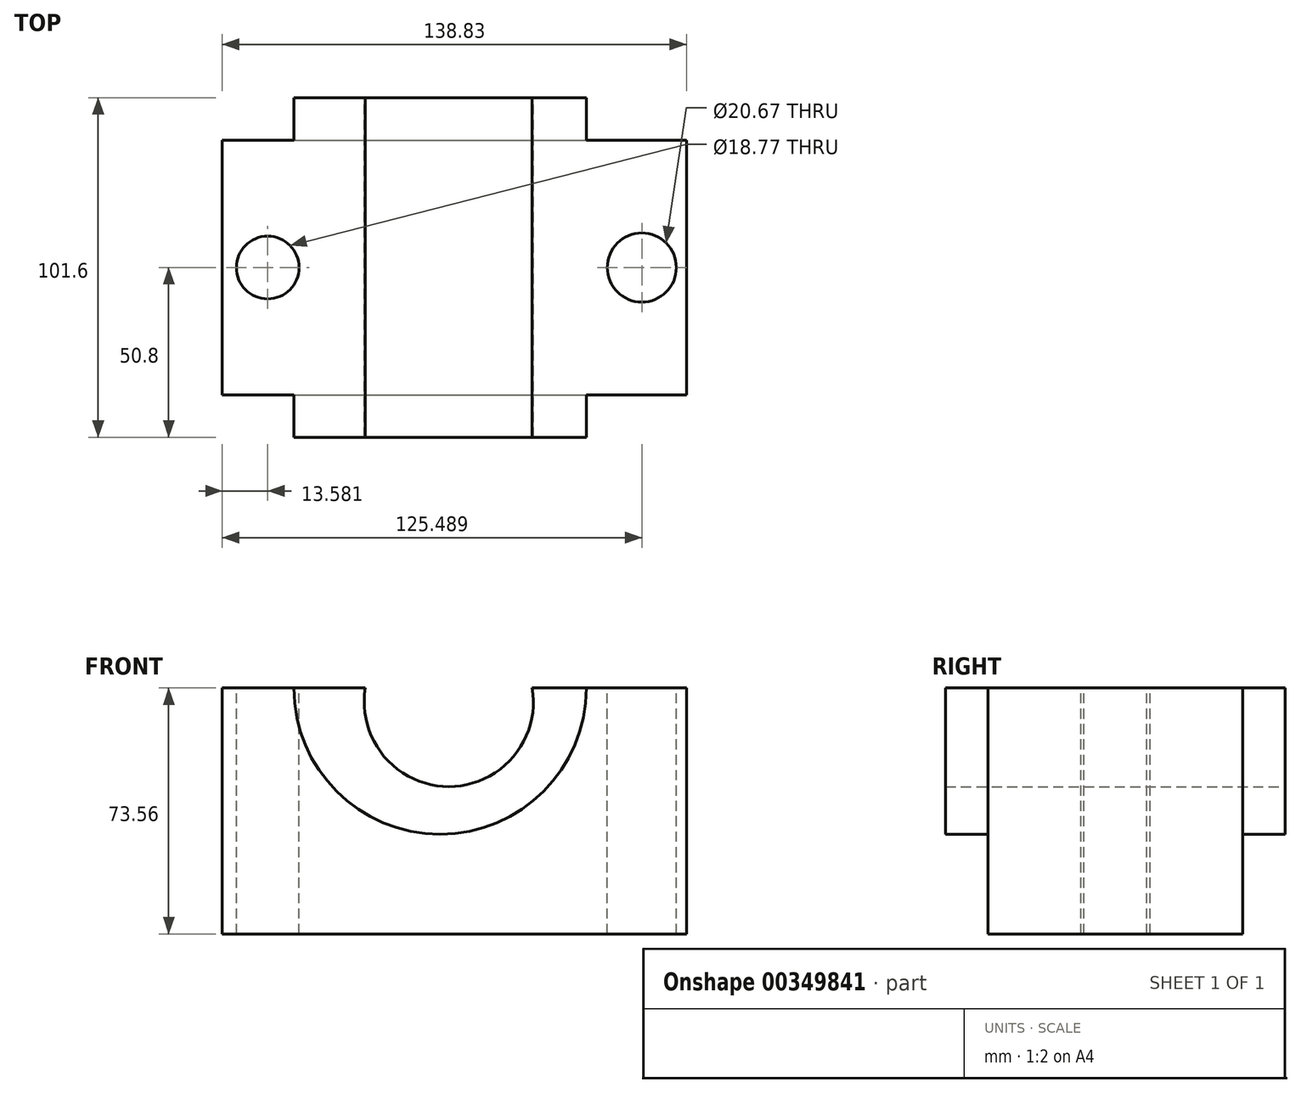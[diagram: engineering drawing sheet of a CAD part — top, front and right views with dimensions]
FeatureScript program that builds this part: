
annotation { "Feature Type Name" : "Feature", "Feature Type Description" : "" }
export const myFeature = defineFeature(function(context is Context, id is Id, definition is map)
    precondition{}
    {
        {
            var Q0;
            Q0=qCreatedBy(makeId("Front.planeOp"),FACE);
            var sketch = newSketch(context, id + "F0", { "sketchPlane" : qUnion([Q0])});
            skLineSegment(sketch, "E0.bottom", {"start": v(-77.5, 11.39) * mm, "end": v(61.33, 11.39) * mm});
            skLineSegment(sketch, "E0.top", {"start": v(-77.5, -62.17) * mm, "end": v(61.33, -62.17) * mm});
            skLineSegment(sketch, "E0.left", {"start": v(-77.5, 11.39) * mm, "end": v(-77.5, -62.17) * mm});
            skLineSegment(sketch, "E0.right", {"start": v(61.33, 11.39) * mm, "end": v(61.33, -62.17) * mm});
            skArc(sketch, "E1", {"start": v(-34.7, 11.39) * mm, "mid": v(-9.75, -18.1) * mm, "end": v(15.21, 11.39) * mm});
            skSolve(sketch);
        }
        {
            var Q0;
            Q0=makeQuery(id+"F0.imprint","IMPRINT",FACE,{"disambiguationData":[TD([[makeQuery(id+"F0.imprint","IMPRINT",EDGE,{"derivedFrom":sQuery(id+"F0.wireOp",EDGE,"E0.top")}),1.0]])]});
            extrude(context, id + "F1", {"entities" : qUnion([Q0]), "depth" : 38.1 * mm, "hasSecondDirection" : true, "secondDirectionOppositeDirection" : true, "secondDirectionDepth" : 38.1 * mm});
        }
        {
            var Q0;
            Q0=qCreatedBy(makeId("Front.planeOp"),FACE);
            var sketch = newSketch(context, id + "F2", { "sketchPlane" : qUnion([Q0])});
            skArc(sketch, "E2.0", {"start": v(-34.7, 11.39) * mm, "mid": v(-9.75, -18.1) * mm, "end": v(15.21, 11.39) * mm});
            skLineSegment(sketch, "E3.0", {"start": v(-77.5, 11.39) * mm, "end": v(-34.7, 11.39) * mm});
            skLineSegment(sketch, "E4.0", {"start": v(15.21, 11.39) * mm, "end": v(61.33, 11.39) * mm});
            skArc(sketch, "E5", {"start": v(-56.1, 11.39) * mm, "mid": v(-12.36, -32.36) * mm, "end": v(31.38, 11.39) * mm});
            skPoint(sketch, "E6", {"position": v(38.27, 11.39) * mm});
            skSolve(sketch);
        }
        {
            var Q0;
            Q0 = qSketchRegion(id + "F2", true);
            extrude(context, id + "F3", {"entities" : qUnion([Q0]), "operationType" : NewBodyOperationType.ADD, "depth" : 50.8 * mm, "hasSecondDirection" : true, "secondDirectionOppositeDirection" : true, "secondDirectionDepth" : 50.8 * mm});
        }
        {
            var Q0;
            {var subQ0=sQuery(id+"F0.wireOp",EDGE,"E0.bottom");Q0=makeQuery(id+"F3.boolean.opBoolean","MERGE",FACE,{"derivedFrom":[makeQuery(id+"F1.opExtrude","SWEPT_FACE",FACE,{"disambiguationData":[OSD([subQ0]),TDD([makeQuery(id+"F0.imprint","IMPRINT",EDGE,{"disambiguationData":[TD([[makeQuery(id+"F0.imprint","INTERSECT",VERTEX,{"derivedFrom":[subQ0,sQuery(id+"F0.wireOp",EDGE,"E0.right")]}),1.0]])],"derivedFrom":subQ0})])]}),makeQuery(id+"F3.opExtrude","SWEPT_FACE",FACE,{"disambiguationData":[OSD([sQuery(id+"F2.wireOp",EDGE,"E4.0")])]})]});}
            var sketch = newSketch(context, id + "F4", { "sketchPlane" : qUnion([Q0])});
            skCircle(sketch, "E7", {"center": v(47.99, 0) * mm, "radius": 10.33 * mm});
            skCircle(sketch, "E8", {"center": v(-63.92, 0) * mm, "radius": 9.38 * mm});
            skSolve(sketch);
        }
        {
            var Q0;
            Q0 = qSketchRegion(id + "F4", true);
            extrude(context, id + "F5", {"entities" : qUnion([Q0]), "operationType" : NewBodyOperationType.REMOVE, "endBound" : BoundingType.THROUGH_ALL, "oppositeDirection" : true, "depth" : 25.4 * mm});
        }
    });
